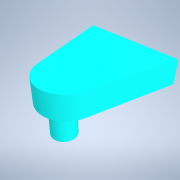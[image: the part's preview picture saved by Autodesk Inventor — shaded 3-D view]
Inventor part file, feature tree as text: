
AUTODESK INVENTOR PART (.ipt)
format: ipt  version: 2022 (Build 260153000, 153)  size: 98,816 bytes
history: imported  units: in
note: dims shown in document units (in); Inventor stores cm internally (conversion verified against a paired STEP export)
features: imported_body x1
ambient origin geometry x8: Origin, YZ Plane, XZ Plane, XY Plane, X Axis, Y Axis, Z Axis, Center Point
bodies: Solid1 (imported_parasolid), Body1 (imported_parasolid)
feature tree (1):
  imported_body  NMx_Import_Brep_tag  [imported B-rep: ~8 faces, bbox_mm=[60.0, 35.0, 52.384414]]
